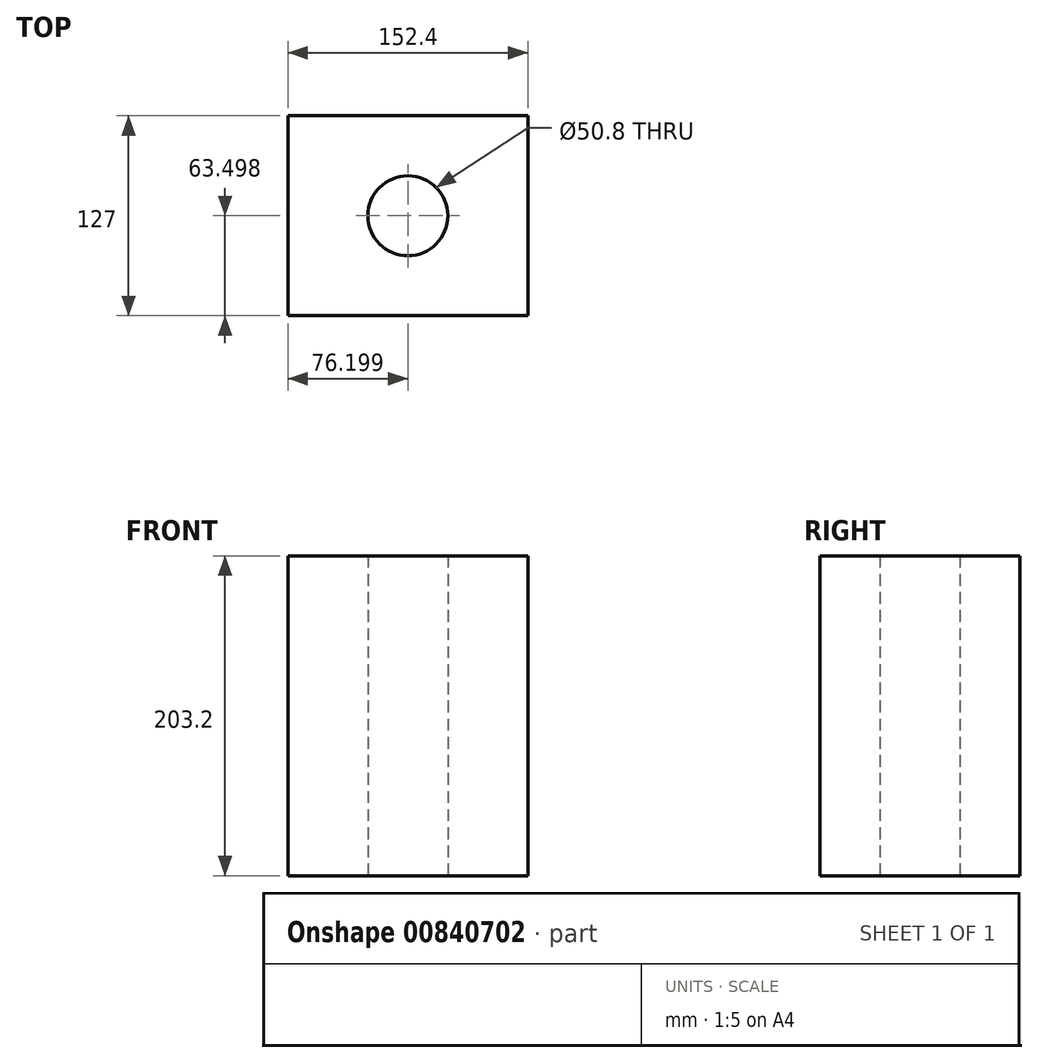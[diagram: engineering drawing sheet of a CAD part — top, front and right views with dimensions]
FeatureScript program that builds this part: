
annotation { "Feature Type Name" : "Feature", "Feature Type Description" : "" }
export const myFeature = defineFeature(function(context is Context, id is Id, definition is map)
    precondition{}
    {
        {
            var Q0;
            Q0=qCreatedBy(makeId("Top.planeOp"),FACE);
            var sketch = newSketch(context, id + "F0", { "sketchPlane" : qUnion([Q0])});
            skLineSegment(sketch, "E0.bottom", {"start": v(-76.2, 70.1) * mm, "end": v(76.2, 70.1) * mm});
            skLineSegment(sketch, "E0.top", {"start": v(-76.2, -56.9) * mm, "end": v(76.2, -56.9) * mm});
            skLineSegment(sketch, "E0.left", {"start": v(-76.2, 70.1) * mm, "end": v(-76.2, -56.9) * mm});
            skLineSegment(sketch, "E0.right", {"start": v(76.2, 70.1) * mm, "end": v(76.2, -56.9) * mm});
            skPoint(sketch, "E0.middle", {"position": v(0, 6.6) * mm});
            skCircle(sketch, "E1", {"center": v(0, 6.6) * mm, "radius": 25.4 * mm});
            skSolve(sketch);
        }
        {
            var Q0;
            Q0=makeQuery(id+"F0.imprint","IMPRINT",FACE,{"disambiguationData":[TD([[makeQuery(id+"F0.imprint","IMPRINT",EDGE,{"derivedFrom":sQuery(id+"F0.wireOp",EDGE,"E0.bottom")}),-1.0]])]});
            extrude(context, id + "F1", {"entities" : qUnion([Q0]), "depth" : 203.2 * mm, "offsetDistance" : 25.4 * mm});
        }
    });
